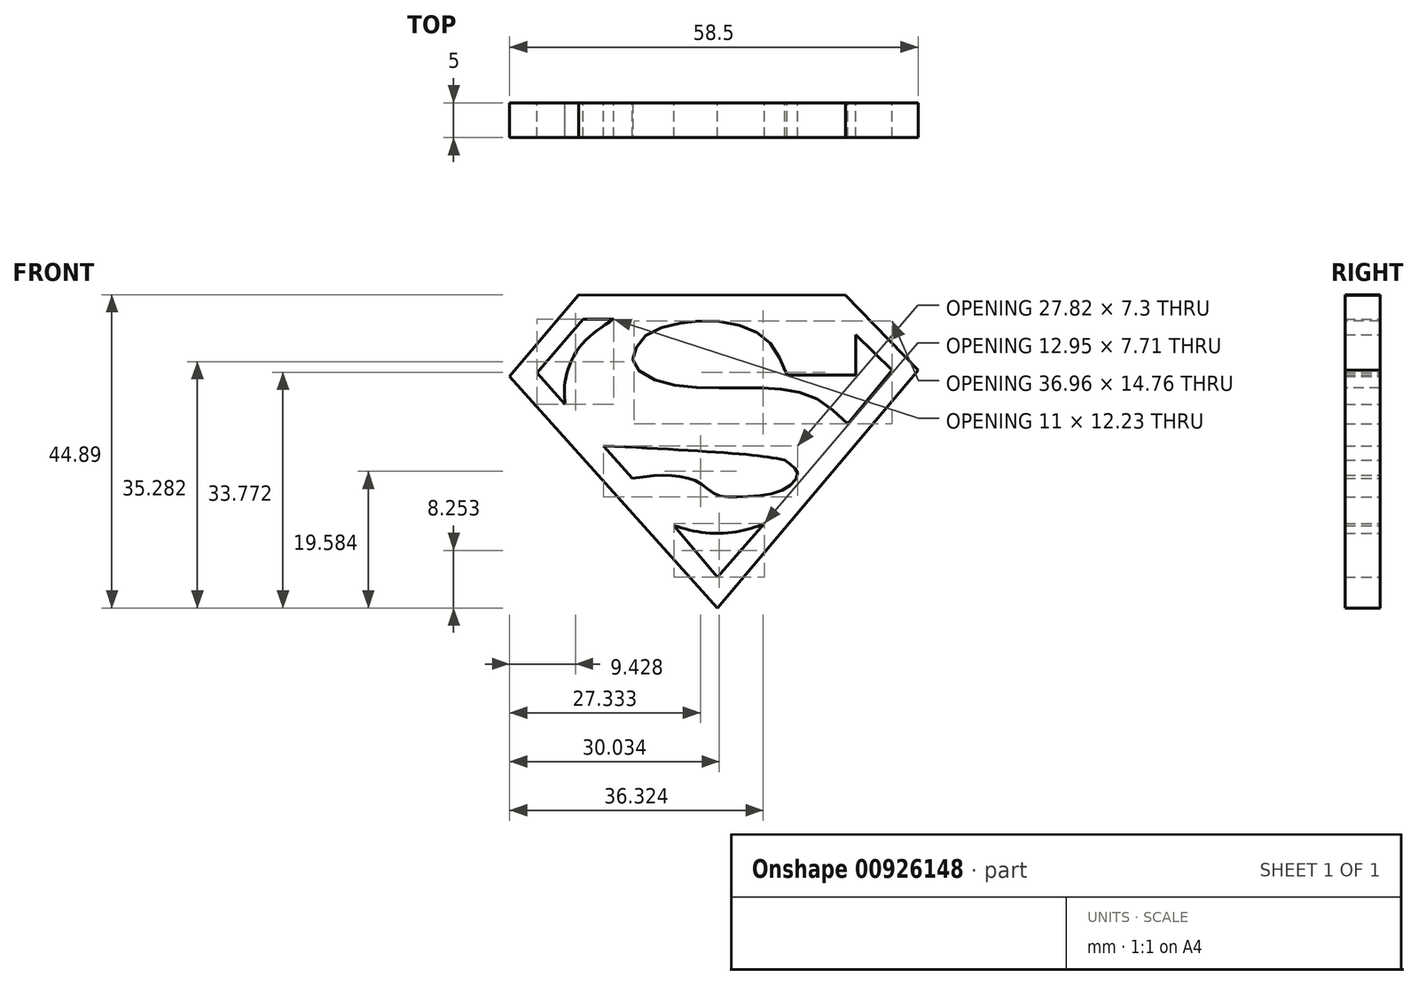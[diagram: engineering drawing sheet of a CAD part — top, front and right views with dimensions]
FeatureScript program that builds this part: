
annotation { "Feature Type Name" : "Feature", "Feature Type Description" : "" }
export const myFeature = defineFeature(function(context is Context, id is Id, definition is map)
    precondition{}
    {
        {
            var Q0;
            Q0=qCreatedBy(makeId("Front.planeOp"),FACE);
            var sketch = newSketch(context, id + "F0", { "sketchPlane" : qUnion([Q0])});
            skLineSegment(sketch, "E0", {"start": v(-30.76, 25.75) * mm, "end": v(-37.34, 18.04) * mm});
            skLineSegment(sketch, "E1", {"start": v(-37.34, 18.04) * mm, "end": v(-33.33, 13.52) * mm});
            skLineSegment(sketch, "E2", {"start": v(-30.76, 25.75) * mm, "end": v(-26.34, 25.75) * mm});
            skLineSegment(sketch, "E3", {"start": v(8.3, 23.49) * mm, "end": v(8.3, 17.73) * mm});
            skLineSegment(sketch, "E4", {"start": v(8.3, 17.73) * mm, "end": v(-1.58, 17.73) * mm});
            skLineSegment(sketch, "E5", {"start": v(8.3, 23.49) * mm, "end": v(13.53, 18.45) * mm});
            skLineSegment(sketch, "E6", {"start": v(13.53, 18.45) * mm, "end": v(7.16, 10.74) * mm});
            skLineSegment(sketch, "E7", {"start": v(-17.71, -3.85) * mm, "end": v(-11.54, -11.25) * mm});
            skLineSegment(sketch, "E8", {"start": v(-11.54, -11.25) * mm, "end": v(-4.76, -3.54) * mm});
            skLineSegment(sketch, "E9", {"start": v(-31.38, 29.24) * mm, "end": v(-41.27, 17.52) * mm});
            skLineSegment(sketch, "E10", {"start": v(-41.27, 17.52) * mm, "end": v(-11.54, -15.65) * mm});
            skLineSegment(sketch, "E11", {"start": v(-11.54, -15.65) * mm, "end": v(17.23, 18.45) * mm});
            skLineSegment(sketch, "E12", {"start": v(17.23, 18.45) * mm, "end": v(6.85, 29.16) * mm});
            skLineSegment(sketch, "E13", {"start": v(6.85, 29.16) * mm, "end": v(-31.38, 29.24) * mm});
            skPoint(sketch, "E14.2.internal.snap0", {"position": v(-34.05, 21.9) * mm});
            skFitSpline(sketch, "E14", {"points": [v(-33.33, 13.52) * mm, v(-33.33, 16.9) * mm, v(-31.11, 21.9) * mm, v(-26.34, 25.75) * mm], "startDerivative": vector(-1.12, 11.55) * mm, "endDerivative": vector(14.11, 9.14) * mm});
            skFitSpline(sketch, "E15", {"points": [v(-1.58, 17.73) * mm, v(-3.62, 21.87) * mm, v(-6.8, 24.3) * mm, v(-12.28, 25.47) * mm, v(-17.46, 25.06) * mm, v(-21.76, 23.37) * mm, v(-23.45, 20.96) * mm, v(-23.4, 19.07) * mm, v(-19.92, 16.82) * mm, v(-13.67, 15.9) * mm, v(-6.75, 15.9) * mm, v(-1.58, 15.59) * mm, v(2.94, 14.2) * mm, v(7.16, 10.74) * mm], "startDerivative": vector(-23.18, 58.32) * mm, "endDerivative": vector(48.7, -46.96) * mm});
            skFitSpline(sketch, "E16", {"points": [v(-17.71, -3.85) * mm, v(-13.37, -4.87) * mm, v(-8.26, -4.66) * mm, v(-4.76, -3.54) * mm], "startDerivative": vector(12.4, -3.76) * mm, "endDerivative": vector(10.73, 4.18) * mm});
            skLineSegment(sketch, "E17", {"start": v(-27.85, 7.58) * mm, "end": v(-23.7, 2.9) * mm});
            skFitSpline(sketch, "E18", {"points": [v(-27.85, 7.58) * mm, v(-7.2, 6.3) * mm, v(-1.87, 5.56) * mm], "startDerivative": vector(36.28, -1.84) * mm, "endDerivative": vector(13.16, -2.25) * mm});
            skFitSpline(sketch, "E19", {"points": [v(-1.87, 5.56) * mm, v(-0.58, 4.53) * mm, v(0, 3.56) * mm, v(-1.04, 1.92) * mm, v(-4.74, 0.54) * mm, v(-9.41, 0.27) * mm, v(-11.5, 0.48) * mm, v(-13.14, 1.6) * mm, v(-14.82, 2.65) * mm, v(-17.11, 3.2) * mm, v(-19.77, 3.38) * mm, v(-23.7, 2.9) * mm], "startDerivative": vector(18.43, -13.8) * mm, "endDerivative": vector(-35.84, -5.76) * mm});
            skSolve(sketch);
        }
        {
            var Q0;
            Q0 = qSketchRegion(id + "F0", true);
            extrude(context, id + "F1", {"entities" : qUnion([Q0]), "depth" : 5 * mm, "offsetDistance" : 25.4 * mm});
        }
    });
